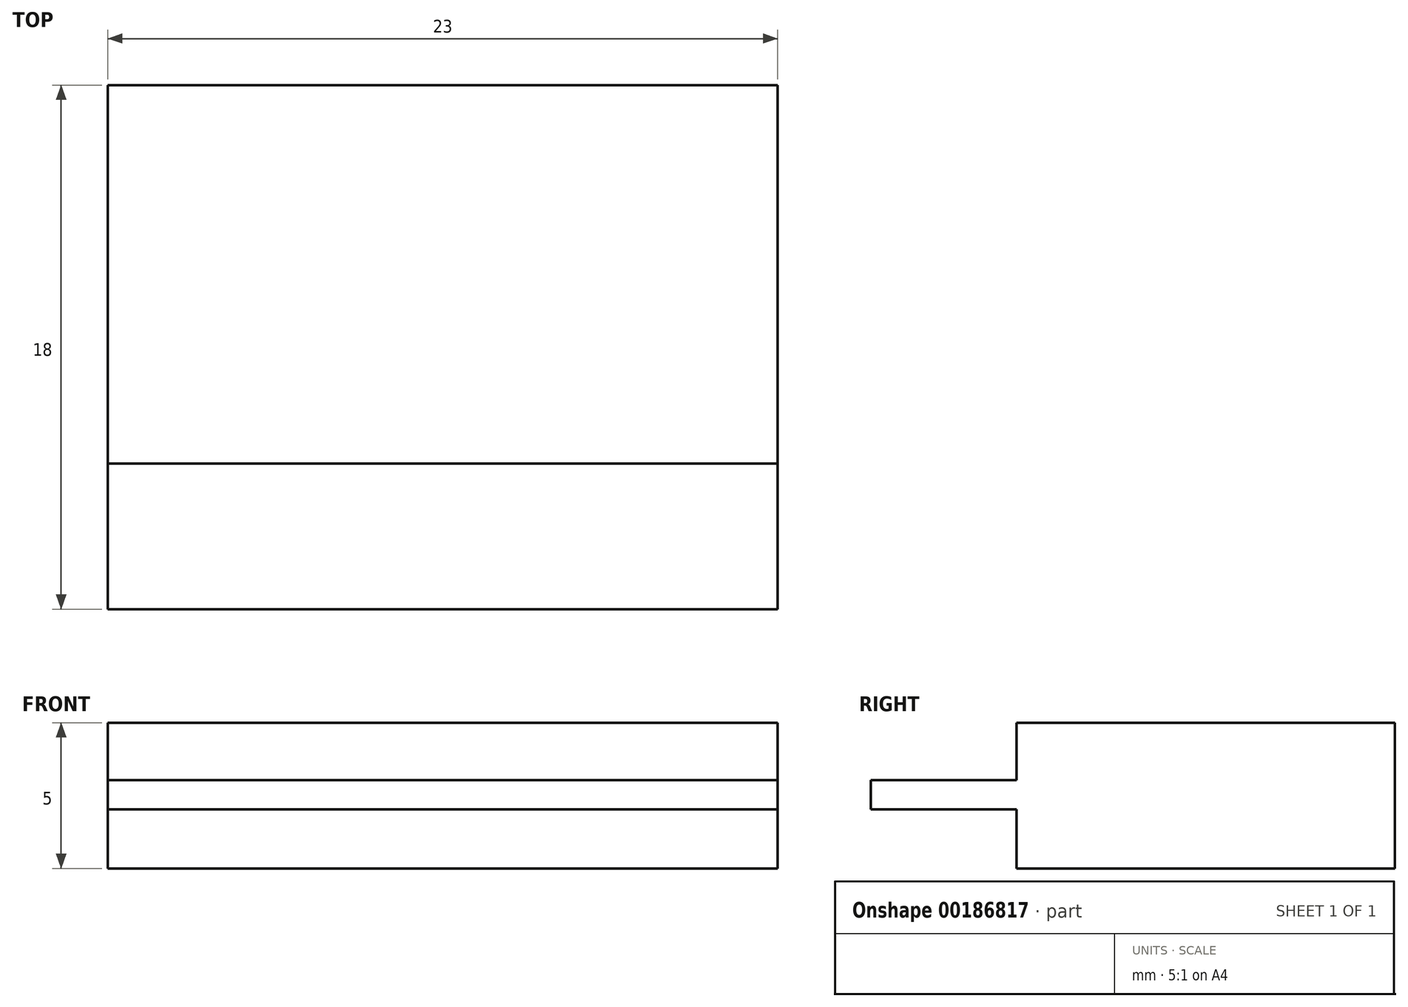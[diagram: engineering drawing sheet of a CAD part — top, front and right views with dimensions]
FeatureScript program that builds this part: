
annotation { "Feature Type Name" : "Feature", "Feature Type Description" : "" }
export const myFeature = defineFeature(function(context is Context, id is Id, definition is map)
    precondition{}
    {
        {
            var Q0;
            Q0=qCreatedBy(makeId("Front.planeOp"),FACE);
            var sketch = newSketch(context, id + "F0", { "sketchPlane" : qUnion([Q0])});
            skLineSegment(sketch, "E0.bottom", {"start": v(-11.5, 2.5) * mm, "end": v(11.5, 2.5) * mm});
            skLineSegment(sketch, "E0.top", {"start": v(-11.5, -2.5) * mm, "end": v(11.5, -2.5) * mm});
            skLineSegment(sketch, "E0.left", {"start": v(-11.5, 2.5) * mm, "end": v(-11.5, -2.5) * mm});
            skLineSegment(sketch, "E0.right", {"start": v(11.5, 2.5) * mm, "end": v(11.5, -2.5) * mm});
            skPoint(sketch, "E0.middle", {"position": v(0, 0) * mm});
            skSolve(sketch);
        }
        {
            var Q0;
            Q0=makeQuery(id+"F0.imprint","IMPRINT",FACE,{"disambiguationData":[TD([[makeQuery(id+"F0.imprint","IMPRINT",EDGE,{"derivedFrom":sQuery(id+"F0.wireOp",EDGE,"E0.bottom")}),-1.0]])]});
            extrude(context, id + "F1", {"entities" : qUnion([Q0]), "depth" : 13 * mm});
        }
        {
            var Q0;
            Q0=makeQuery(id+"F1.opExtrude","CAP_FACE",FACE,{"disambiguationData":[OSD([sQuery(id+"F0.wireOp",EDGE,"E0.bottom"),sQuery(id+"F0.wireOp",EDGE,"E0.top"),sQuery(id+"F0.wireOp",EDGE,"E0.left"),sQuery(id+"F0.wireOp",EDGE,"E0.right")])],"isStart":false});
            var sketch = newSketch(context, id + "F2", { "sketchPlane" : qUnion([Q0])});
            skLineSegment(sketch, "E1.bottom", {"start": v(-11.5, 0.53) * mm, "end": v(11.5, 0.53) * mm});
            skLineSegment(sketch, "E1.top", {"start": v(-11.5, -0.47) * mm, "end": v(11.5, -0.47) * mm});
            skLineSegment(sketch, "E1.left", {"start": v(-11.5, 0.53) * mm, "end": v(-11.5, -0.47) * mm});
            skLineSegment(sketch, "E1.right", {"start": v(11.5, 0.53) * mm, "end": v(11.5, -0.47) * mm});
            skSolve(sketch);
        }
        {
            var Q0;
            Q0=makeQuery(id+"F2.imprint","IMPRINT",FACE,{"disambiguationData":[TD([[makeQuery(id+"F2.imprint","IMPRINT",EDGE,{"derivedFrom":sQuery(id+"F2.wireOp",EDGE,"E1.bottom")}),-1.0]])]});
            extrude(context, id + "F3", {"entities" : qUnion([Q0]), "operationType" : NewBodyOperationType.ADD, "depth" : 5 * mm});
        }
    });
